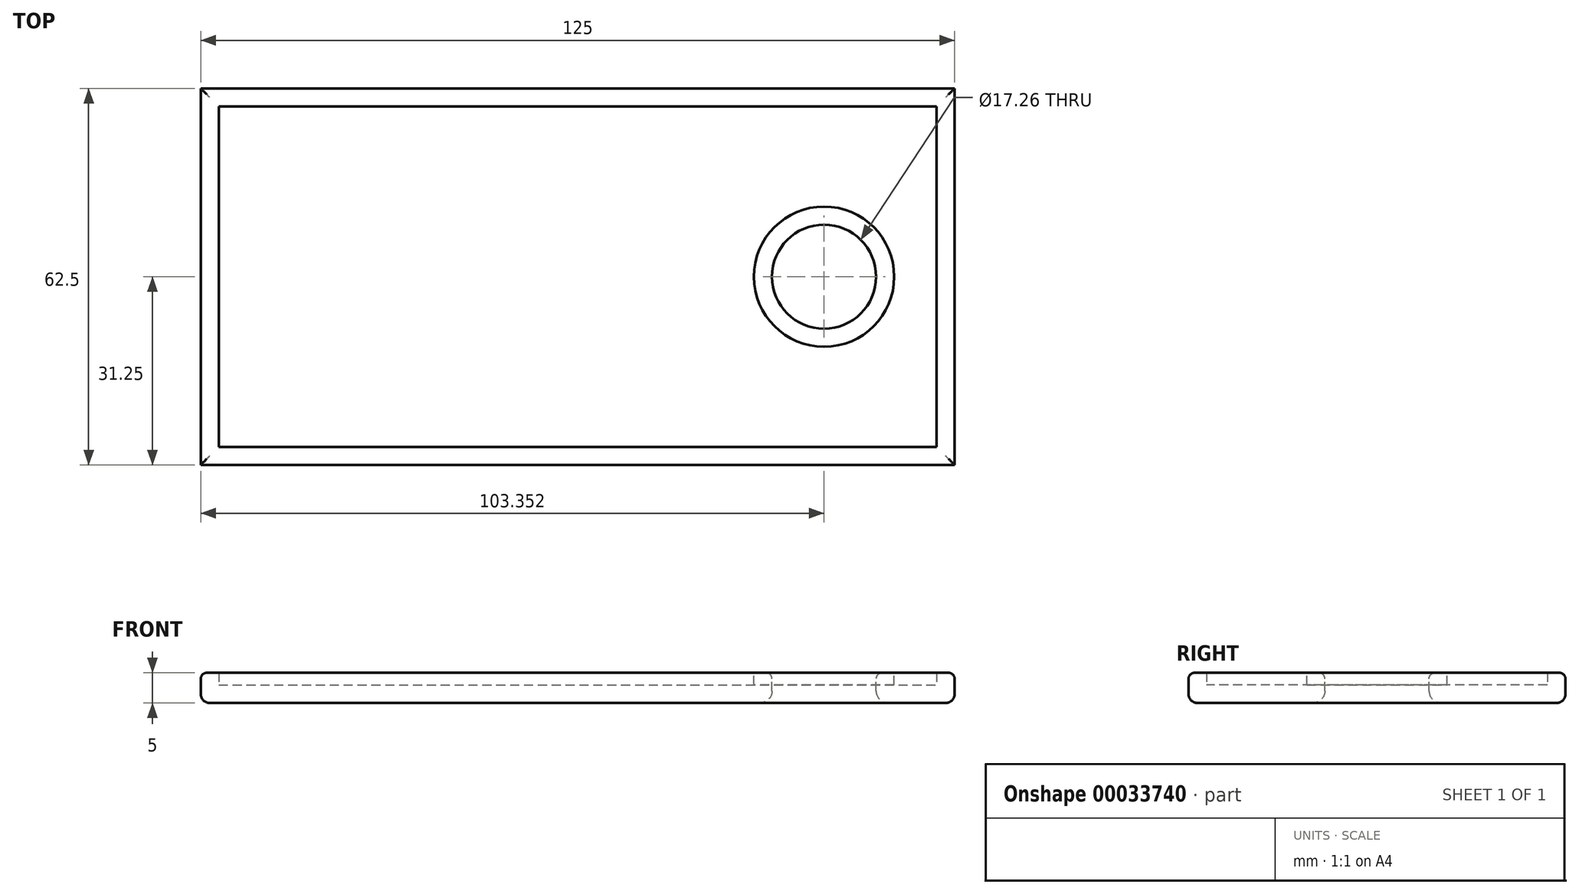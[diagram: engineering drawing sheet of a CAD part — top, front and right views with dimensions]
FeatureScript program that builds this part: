
annotation { "Feature Type Name" : "Feature", "Feature Type Description" : "" }
export const myFeature = defineFeature(function(context is Context, id is Id, definition is map)
    precondition{}
    {
        {
            var Q0;
            Q0=qCreatedBy(makeId("Top.planeOp"),FACE);
            var sketch = newSketch(context, id + "F0", { "sketchPlane" : qUnion([Q0])});
            skLineSegment(sketch, "E0.rect.bottom", {"start": v(62.5, 31.25) * mm, "end": v(-62.5, 31.25) * mm});
            skLineSegment(sketch, "E0.rect.top", {"start": v(62.5, -31.25) * mm, "end": v(-62.5, -31.25) * mm});
            skLineSegment(sketch, "E0.rect.left", {"start": v(62.5, 31.25) * mm, "end": v(62.5, -31.25) * mm});
            skLineSegment(sketch, "E0.rect.right", {"start": v(-62.5, 31.25) * mm, "end": v(-62.5, -31.25) * mm});
            skPoint(sketch, "E0.rect.middle", {"position": v(0, 0) * mm});
            skSolve(sketch);
        }
        {
            var Q0;
            Q0 = qSketchRegion(id + "F0", true);
            extrude(context, id + "F1", {"entities" : qUnion([Q0]), "depth" : 5 * mm});
        }
        {
            var Q0;
            Q0=makeQuery(id+"F1.opExtrude","CAP_FACE",FACE,{"disambiguationData":[OSD([sQuery(id+"F0.wireOp",EDGE,"E0.rect.bottom"),sQuery(id+"F0.wireOp",EDGE,"E0.rect.top"),sQuery(id+"F0.wireOp",EDGE,"E0.rect.left"),sQuery(id+"F0.wireOp",EDGE,"E0.rect.right")])],"isStart":false});
            var sketch = newSketch(context, id + "F6", { "sketchPlane" : qUnion([Q0])});
            skCircle(sketch, "E1", {"center": v(40.85, 0) * mm, "radius": 8.63 * mm});
            skSolve(sketch);
        }
        {
            var Q0;
            Q0 = qSketchRegion(id + "F6", true);
            extrude(context, id + "F7", {"entities" : qUnion([Q0]), "operationType" : NewBodyOperationType.REMOVE, "oppositeDirection" : true, "depth" : 25 * mm});
        }
        {
            var Q0;
            Q0=makeQuery(id+"F7.boolean.opBoolean","COPY",EDGE,{"derivedFrom":makeQuery(id+"F7.opExtrude","CAP_EDGE",EDGE,{"disambiguationData":[OSD([sQuery(id+"F6.wireOp",EDGE,"E1")])],"isStart":true})});
            var Q1;
            Q1=makeQuery(id+"F1.opExtrude","CAP_FACE",FACE,{"disambiguationData":[OSD([sQuery(id+"F0.wireOp",EDGE,"E0.rect.bottom"),sQuery(id+"F0.wireOp",EDGE,"E0.rect.top"),sQuery(id+"F0.wireOp",EDGE,"E0.rect.left"),sQuery(id+"F0.wireOp",EDGE,"E0.rect.right")])],"isStart":false});
            fillet(context, id + "F2", {"entities" : qUnion([Q0, Q1]), "radius" : 1 * mm, "tangentPropagation" : true, "allowEdgeOverflow" : false});
        }
        {
            var Q0;
            Q0=makeQuery(id+"F1.opExtrude","CAP_EDGE",EDGE,{"disambiguationData":[OSD([sQuery(id+"F0.wireOp",EDGE,"E0.rect.bottom")])],"isStart":true});
            var Q1;
            Q1=makeQuery(id+"F1.opExtrude","CAP_EDGE",EDGE,{"disambiguationData":[OSD([sQuery(id+"F0.wireOp",EDGE,"E0.rect.left")])],"isStart":true});
            var Q2;
            Q2=makeQuery(id+"F1.opExtrude","CAP_EDGE",EDGE,{"disambiguationData":[OSD([sQuery(id+"F0.wireOp",EDGE,"E0.rect.top")])],"isStart":true});
            var Q3;
            Q3=makeQuery(id+"F1.opExtrude","CAP_EDGE",EDGE,{"disambiguationData":[OSD([sQuery(id+"F0.wireOp",EDGE,"E0.rect.right")])],"isStart":true});
            fillet(context, id + "F3", {"entities" : qUnion([Q0, Q1, Q2, Q3]), "radius" : 1.5 * mm, "tangentPropagation" : true, "allowEdgeOverflow" : false});
        }
        {
            var Q0;
            Q0=makeQuery(id+"F7.boolean.opBoolean","INTERSECT",EDGE,{"derivedFrom":[makeQuery(id+"F1.opExtrude","CAP_FACE",FACE,{"disambiguationData":[OSD([sQuery(id+"F0.wireOp",EDGE,"E0.rect.bottom"),sQuery(id+"F0.wireOp",EDGE,"E0.rect.top"),sQuery(id+"F0.wireOp",EDGE,"E0.rect.left"),sQuery(id+"F0.wireOp",EDGE,"E0.rect.right")])],"isStart":true}),makeQuery(id+"F7.opExtrude","SWEPT_FACE",FACE,{"disambiguationData":[OSD([sQuery(id+"F6.wireOp",EDGE,"E1")])]})]});
            fillet(context, id + "F4", {"entities" : qUnion([Q0]), "radius" : 2 * mm, "tangentPropagation" : true, "allowEdgeOverflow" : false});
        }
        {
            var Q0;
            Q0=makeQuery(id+"F1.opExtrude","CAP_FACE",FACE,{"disambiguationData":[OSD([sQuery(id+"F0.wireOp",EDGE,"E0.rect.bottom"),sQuery(id+"F0.wireOp",EDGE,"E0.rect.top"),sQuery(id+"F0.wireOp",EDGE,"E0.rect.left"),sQuery(id+"F0.wireOp",EDGE,"E0.rect.right")])],"isStart":false});
            shell(context, id + "F5", {"entities" : qUnion([Q0]), "thickness" : 3 * mm});
        }
    });
